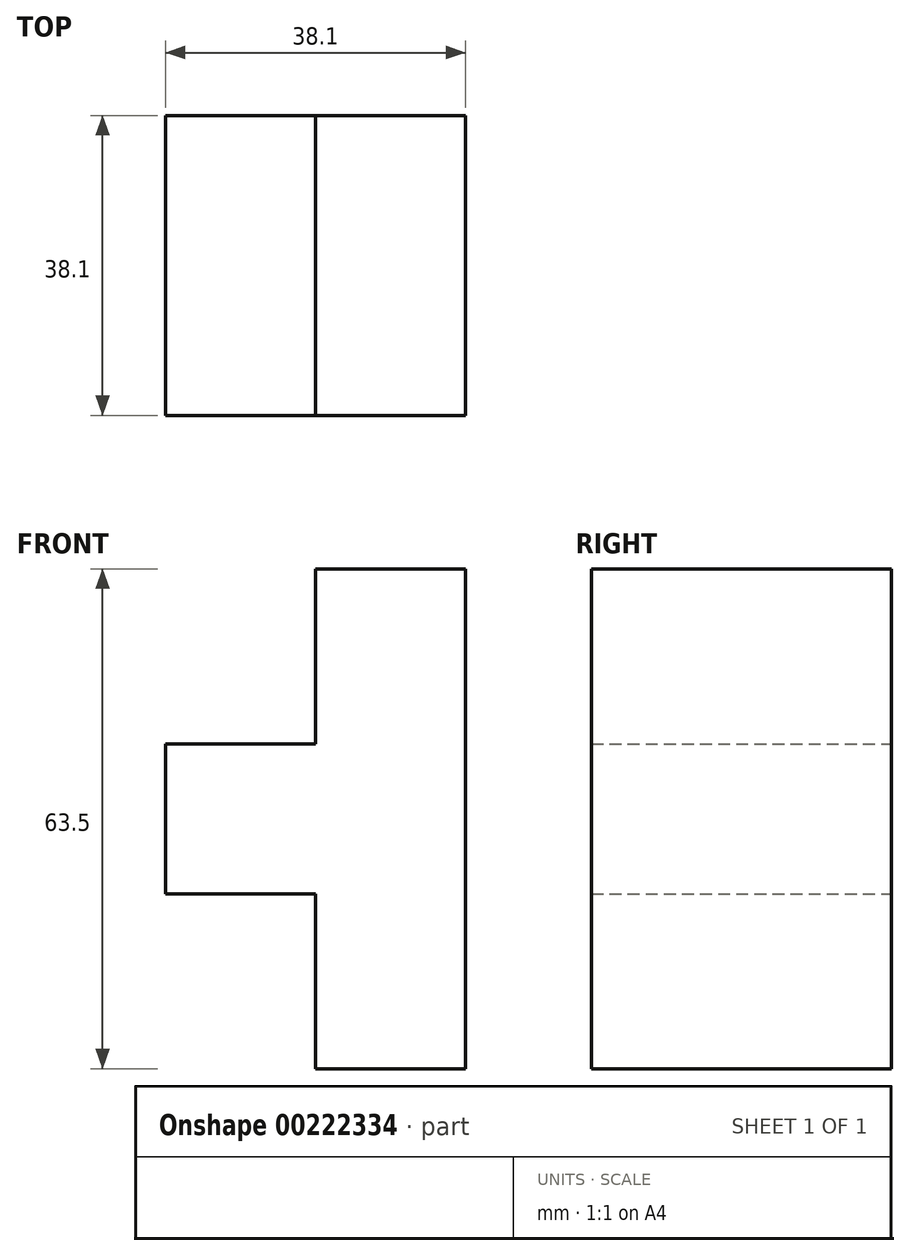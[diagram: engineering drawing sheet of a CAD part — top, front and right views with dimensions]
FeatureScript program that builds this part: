
annotation { "Feature Type Name" : "Feature", "Feature Type Description" : "" }
export const myFeature = defineFeature(function(context is Context, id is Id, definition is map)
    precondition{}
    {
        {
            var Q0;
            Q0=qCreatedBy(makeId("Front.planeOp"),FACE);
            var sketch = newSketch(context, id + "F0", { "sketchPlane" : qUnion([Q0])});
            skLineSegment(sketch, "E0.bottom", {"start": v(-37.77, 7.58) * mm, "end": v(-56.82, 7.58) * mm});
            skLineSegment(sketch, "E0.top", {"start": v(-37.77, 71.08) * mm, "end": v(-56.82, 71.08) * mm});
            skLineSegment(sketch, "E0.left", {"start": v(-37.77, 7.58) * mm, "end": v(-37.77, 71.08) * mm});
            skLineSegment(sketch, "E0.right", {"start": v(-56.82, 7.58) * mm, "end": v(-56.82, 71.08) * mm});
            skPoint(sketch, "E0.middle", {"position": v(-47.3, 39.33) * mm});
            skLineSegment(sketch, "E1.bottom", {"start": v(-56.82, 29.8) * mm, "end": v(-75.87, 29.8) * mm});
            skLineSegment(sketch, "E1.top", {"start": v(-56.82, 48.86) * mm, "end": v(-75.87, 48.86) * mm});
            skLineSegment(sketch, "E1.left", {"start": v(-56.82, 29.8) * mm, "end": v(-56.82, 48.86) * mm});
            skLineSegment(sketch, "E1.right", {"start": v(-75.87, 29.8) * mm, "end": v(-75.87, 48.86) * mm});
            skPoint(sketch, "E1.middle", {"position": v(-66.35, 39.33) * mm});
            skPoint(sketch, "E2.endSnap0", {"position": v(-56.82, 39.33) * mm});
            skSolve(sketch);
        }
        {
            var Q0;
            Q0=qSketchRegion(id+"F0",true);
            extrude(context, id + "F1", {"entities" : qUnion([Q0]), "depth" : 25.4 * mm});
        }
        {
            var Q0;
            Q0=qSketchRegion(id+"F0",true);
            extrude(context, id + "F2", {"entities" : qUnion([Q0]), "operationType" : NewBodyOperationType.ADD, "endBound" : BoundingType.SYMMETRIC, "depth" : 25.4 * mm});
        }
    });
